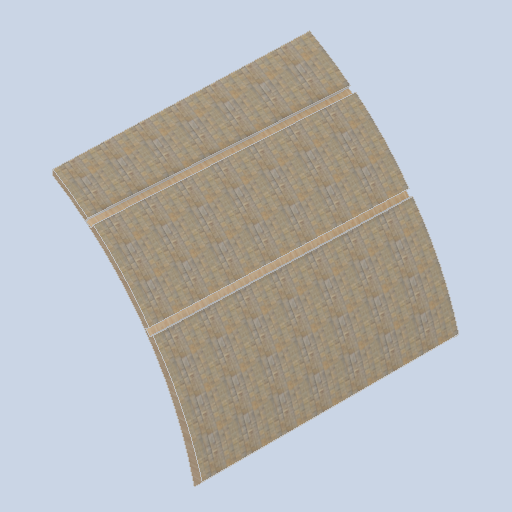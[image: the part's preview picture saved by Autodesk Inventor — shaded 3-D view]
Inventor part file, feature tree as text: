
AUTODESK INVENTOR PART (.ipt)
format: ipt  version: 2024.2 (Build 282272000, 272)  size: 355,328 bytes
history: native  units: in
note: dims shown in document units (in); Inventor stores cm internally (conversion verified against a paired STEP export)
features: other x3, sketch x2, plane x2
ambient origin geometry x8: Origin, YZ Plane, XZ Plane, XY Plane, X Axis, Y Axis, Z Axis, Center Point
bodies: Solid1 (feature_tree)
feature tree (7):
  other  "panel_block_03.ipt"
  other  "Solid1::panel_block_03.ipt"
  other  "TaggingFeature1"
  sketch  "Sketch1"  dims[d0=0.3937in]
  sketch  "Sketch2"
  plane  "Work Plane1"
  plane  "Work Plane2"
